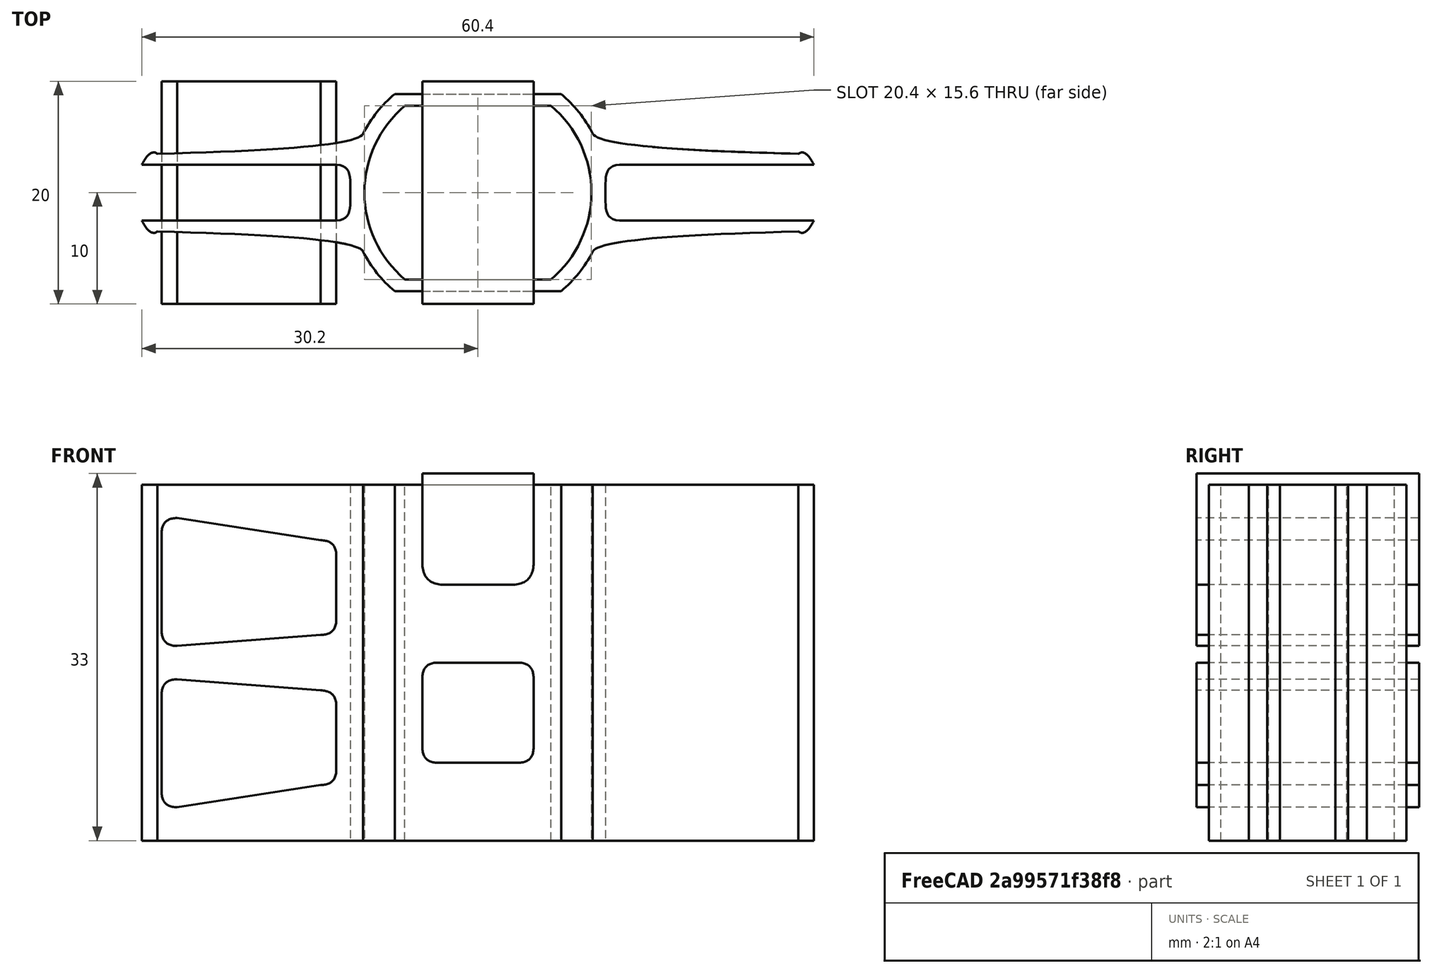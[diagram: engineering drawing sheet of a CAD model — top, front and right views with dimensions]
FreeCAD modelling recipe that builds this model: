
FCSTD DOCUMENT  (FreeCAD 0.19R0.19.2)
Label: 026
License: All rights reserved
LicenseURL: http://en.wikipedia.org/wiki/All_rights_reserved
objects: Sketcher::SketchObject×3, Part::Extrusion×3
note: 6 computed .brp shape members not serialized (recipe doc carries the construction recipe); baked Part::Feature solids carry a one-line shape summary decoded from their .brp

FEATURE [Sketcher::SketchObject] Sketch  label="main001"
  FullyConstrained = true
  sketch-geometry (80):
    g0: ArcOfCircle CenterX=-3.45031e-07 CenterY=0 CenterZ=0 NormalX=0 NormalY=0 NormalZ=1 AngleXU=0 Radius=10.2 StartAngle=5.4126 EndAngle=7.15377
    g1: ArcOfCircle CenterX=-3.45031e-07 CenterY=0 CenterZ=0 NormalX=0 NormalY=0 NormalZ=1 AngleXU=0 Radius=10.2 StartAngle=2.27101 EndAngle=4.01218
    g2: LineSegment StartX=-6.57267 StartY=7.8 StartZ=0 EndX=6.57267 EndY=7.8 EndZ=0
    g3: LineSegment StartX=-6.57267 StartY=-7.8 StartZ=0 EndX=6.57267 EndY=-7.8 EndZ=0
    g4: ArcOfCircle CenterX=-3.45031e-07 CenterY=0 CenterZ=0 NormalX=0 NormalY=0 NormalZ=1 AngleXU=0 Radius=11.6 StartAngle=2.27101 EndAngle=2.66709
    g5: ArcOfCircle CenterX=-3.45031e-07 CenterY=0 CenterZ=0 NormalX=0 NormalY=0 NormalZ=1 AngleXU=0 Radius=11.6 StartAngle=5.4126 EndAngle=5.80868
    g6: LineSegment StartX=-7.4748 StartY=8.87059 StartZ=0 EndX=7.4748 EndY=8.87059 EndZ=0
    g7: LineSegment StartX=-7.4748 StartY=-8.87059 StartZ=0 EndX=7.4748 EndY=-8.87059 EndZ=0
    g8: ArcOfCircle CenterX=-3.45031e-07 CenterY=0 CenterZ=0 NormalX=0 NormalY=0 NormalZ=1 AngleXU=0 Radius=11.6 StartAngle=3.6161 EndAngle=4.01218
    g9: ArcOfCircle CenterX=-3.45031e-07 CenterY=0 CenterZ=0 NormalX=0 NormalY=0 NormalZ=1 AngleXU=0 Radius=11.6 StartAngle=0.474503 EndAngle=0.870585
    g10: Circle CenterX=-28.8 CenterY=3.5 CenterZ=0 NormalX=0 NormalY=0 NormalZ=1 AngleXU=0 Radius=1
    g11: Circle CenterX=-10.9247 CenterY=3.9 CenterZ=0 NormalX=0 NormalY=0 NormalZ=1 AngleXU=0 Radius=1
    g12: Circle CenterX=-10.3184 CenterY=5.3 CenterZ=0 NormalX=0 NormalY=0 NormalZ=1 AngleXU=0 Radius=1
    g13: BSplineCurve PolesCount=3 KnotsCount=2 Degree=2 IsPeriodic=0
    g14: GeomPoint X=-28.8 Y=3.5 Z=0
    g15: GeomPoint X=-10.3184 Y=5.3 Z=0
    g16: Circle CenterX=28.8 CenterY=3.5 CenterZ=0 NormalX=0 NormalY=0 NormalZ=1 AngleXU=0 Radius=1
    g17: Circle CenterX=10.9247 CenterY=3.9 CenterZ=0 NormalX=0 NormalY=0 NormalZ=1 AngleXU=0 Radius=1
    g18: Circle CenterX=10.3184 CenterY=5.3 CenterZ=0 NormalX=0 NormalY=0 NormalZ=1 AngleXU=0 Radius=1
    g19: BSplineCurve PolesCount=3 KnotsCount=2 Degree=2 IsPeriodic=0
    g20: GeomPoint X=28.8 Y=3.5 Z=0
    g21: GeomPoint X=10.3184 Y=5.3 Z=0
    g22: Circle CenterX=-28.8 CenterY=-3.5 CenterZ=0 NormalX=0 NormalY=0 NormalZ=1 AngleXU=0 Radius=1
    g23: Circle CenterX=-10.9247 CenterY=-3.9 CenterZ=0 NormalX=0 NormalY=0 NormalZ=1 AngleXU=0 Radius=1
    g24: Circle CenterX=-10.3184 CenterY=-5.3 CenterZ=0 NormalX=0 NormalY=0 NormalZ=1 AngleXU=0 Radius=1
    g25: BSplineCurve PolesCount=3 KnotsCount=2 Degree=2 IsPeriodic=0
    g26: GeomPoint X=-28.8 Y=-3.5 Z=0
    g27: GeomPoint X=-10.3184 Y=-5.3 Z=0
    g28: Circle CenterX=28.8 CenterY=-3.5 CenterZ=0 NormalX=0 NormalY=0 NormalZ=1 AngleXU=0 Radius=1
    g29: Circle CenterX=10.9247 CenterY=-3.9 CenterZ=0 NormalX=0 NormalY=0 NormalZ=1 AngleXU=0 Radius=1
    g30: Circle CenterX=10.3184 CenterY=-5.3 CenterZ=0 NormalX=0 NormalY=0 NormalZ=1 AngleXU=0 Radius=1
    g31: BSplineCurve PolesCount=3 KnotsCount=2 Degree=2 IsPeriodic=0
    g32: GeomPoint X=28.8 Y=-3.5 Z=0
    g33: GeomPoint X=10.3184 Y=-5.3 Z=0
    g34-g38: Circle x5 (B-spline internal-alignment scaffolding for g39; pole/knot coordinates omitted)
    g39: BSplineCurve PolesCount=5 KnotsCount=3 Degree=3 IsPeriodic=0
    g40: GeomPoint X=12.7274 Y=2.5 Z=0
    g41: GeomPoint X=11.4637 Y=2.49999e-07 Z=0
    g42: GeomPoint X=12.7274 Y=-2.5 Z=0
    g43-g47: Circle x5 (B-spline internal-alignment scaffolding for g48; pole/knot coordinates omitted)
    g48: BSplineCurve PolesCount=5 KnotsCount=3 Degree=3 IsPeriodic=0
    g49: GeomPoint X=-12.7274 Y=2.5 Z=0
    g50: GeomPoint X=-11.4637 Y=2.50004e-07 Z=0
    g51: GeomPoint X=-12.7274 Y=-2.5 Z=0
    g52: LineSegment StartX=-30.2 StartY=-2.5 StartZ=0 EndX=-12.7274 EndY=-2.5 EndZ=0
    g53: LineSegment StartX=-30.2 StartY=2.5 StartZ=0 EndX=-12.7274 EndY=2.5 EndZ=0
    g54: LineSegment StartX=30.2 StartY=2.5 StartZ=0 EndX=12.7274 EndY=2.5 EndZ=0
    g55: LineSegment StartX=30.2 StartY=-2.5 StartZ=0 EndX=12.7274 EndY=-2.5 EndZ=0
    g56: Circle CenterX=-30.2 CenterY=2.5 CenterZ=0 NormalX=0 NormalY=0 NormalZ=1 AngleXU=0 Radius=1
    g57: Circle CenterX=-29.4304 CenterY=3.99253 CenterZ=0 NormalX=0 NormalY=0 NormalZ=1 AngleXU=0 Radius=1
    g58: Circle CenterX=-28.8 CenterY=3.5 CenterZ=0 NormalX=0 NormalY=0 NormalZ=1 AngleXU=0 Radius=1
    g59: BSplineCurve PolesCount=3 KnotsCount=2 Degree=2 IsPeriodic=0
    g60: GeomPoint X=-30.2 Y=2.5 Z=0
    g61: GeomPoint X=-28.8 Y=3.5 Z=0
    g62: Circle CenterX=30.2 CenterY=-2.5 CenterZ=0 NormalX=0 NormalY=0 NormalZ=1 AngleXU=0 Radius=1
    g63: Circle CenterX=29.4304 CenterY=-3.99253 CenterZ=0 NormalX=0 NormalY=0 NormalZ=1 AngleXU=0 Radius=1
    g64: Circle CenterX=28.8 CenterY=-3.5 CenterZ=0 NormalX=0 NormalY=0 NormalZ=1 AngleXU=0 Radius=1
    g65: BSplineCurve PolesCount=3 KnotsCount=2 Degree=2 IsPeriodic=0
    g66: GeomPoint X=30.2 Y=-2.5 Z=0
    g67: GeomPoint X=28.8 Y=-3.5 Z=0
    g68: Circle CenterX=30.2 CenterY=2.5 CenterZ=0 NormalX=0 NormalY=0 NormalZ=1 AngleXU=0 Radius=1
    g69: Circle CenterX=29.4304 CenterY=3.99253 CenterZ=0 NormalX=0 NormalY=0 NormalZ=1 AngleXU=0 Radius=1
    g70: Circle CenterX=28.8 CenterY=3.5 CenterZ=0 NormalX=0 NormalY=0 NormalZ=1 AngleXU=0 Radius=1
    g71: BSplineCurve PolesCount=3 KnotsCount=2 Degree=2 IsPeriodic=0
    g72: GeomPoint X=30.2 Y=2.5 Z=0
    g73: GeomPoint X=28.8 Y=3.5 Z=0
    g74: Circle CenterX=-30.2 CenterY=-2.5 CenterZ=0 NormalX=0 NormalY=0 NormalZ=1 AngleXU=0 Radius=1
    g75: Circle CenterX=-29.4304 CenterY=-3.99253 CenterZ=0 NormalX=0 NormalY=0 NormalZ=1 AngleXU=0 Radius=1
    g76: Circle CenterX=-28.8 CenterY=-3.5 CenterZ=0 NormalX=0 NormalY=0 NormalZ=1 AngleXU=0 Radius=1
    g77: BSplineCurve PolesCount=3 KnotsCount=2 Degree=2 IsPeriodic=0
    g78: GeomPoint X=-30.2 Y=-2.5 Z=0
    g79: GeomPoint X=-28.8 Y=-3.5 Z=0
  constraints (131):
    c: Block(g0)
    c: Equal(g0,g1)
    c: Coincident(g0,g1)
    c: Coincident(g2,g1)
    c: Coincident(g2,g0)
    c: Horizontal(g2)
    c: Coincident(g3,g1)
    c: Coincident(g3,g0)
    c: Horizontal(g3)
    c: Block(g2)
    c: Block(g3)
    c: Coincident(g4,g0)
    c: Coincident(g5,g0)
    c: Block(g5)
    c: Block(g4)
    c: Coincident(g6,g4)
    c: Coincident(g6,g9)
    c: Horizontal(g6)
    c: Coincident(g7,g8)
    c: Coincident(g7,g5)
    c: Horizontal(g7)
    c: Equal(g4,g8)
    c: Coincident(g4,g8)
    c: Equal(g5,g9)
    c: Coincident(g5,g9)
    c: Block(g8)
    c: Block(g9)
    c: Weight(g10) = 1
    c: Equal(g10,g11)
    c: Equal(g10,g12)
    c: Coincident(g13,g4)
    c: InternalAlignment(g10,g13)
    c: InternalAlignment(g11,g13)
    c: InternalAlignment(g12,g13)
    c: InternalAlignment(g14,g13)
    c: InternalAlignment(g15,g13)
    c: Weight(g16) = 1
    c: Equal(g16,g17)
    c: Equal(g16,g18)
    c: Coincident(g19,g9)
    c: InternalAlignment(g16,g19)
    c: InternalAlignment(g17,g19)
    c: InternalAlignment(g18,g19)
    c: InternalAlignment(g20,g19)
    c: InternalAlignment(g21,g19)
    c: Weight(g22) = 1
    c: Equal(g22,g23)
    c: Equal(g22,g24)
    c: Coincident(g25,g8)
    c: InternalAlignment(g22,g25)
    c: InternalAlignment(g23,g25)
    c: InternalAlignment(g24,g25)
    c: InternalAlignment(g26,g25)
    c: InternalAlignment(g27,g25)
    c: Weight(g28) = 1
    c: Equal(g28,g29)
    c: Equal(g28,g30)
    c: Coincident(g31,g5)
    c: InternalAlignment(g28,g31)
    c: InternalAlignment(g29,g31)
    c: InternalAlignment(g30,g31)
    c: InternalAlignment(g32,g31)
    c: InternalAlignment(g33,g31)
    c: Block(g19)
    c: Block(g13)
    c: Block(g31)
    c: Block(g25)
    c: Weight(g34) = 1
    c: Equal(g34, g35-g38) x4
    c: InternalAlignment(g34-g38 -> g39) x5
    c: InternalAlignment(g40,g39)
    c: InternalAlignment(g41,g39)
    c: InternalAlignment(g42,g39)
    c: Weight(g43) = 1
    c: Equal(g43,g44)
    c: Equal(g43,g45)
    c: Equal(g43,g46)
    c: InternalAlignment(g43-g47 -> g48) x5
    c: InternalAlignment(g49,g48)
    c: InternalAlignment(g50,g48)
    c: InternalAlignment(g51,g48)
    c: Block(g48)
    c: Block(g39)
    c: Coincident(g52,g48)
    c: Tangent(g52,g22)
    c: Coincident(g53,g48)
    c: Tangent(g53,g10)
    c: Coincident(g54,g39)
    c: Tangent(g54,g16)
    c: Coincident(g55,g39)
    c: Tangent(g55,g28)
    c: Weight(g56) = 1
    c: Equal(g56,g57)
    c: Equal(g56,g58)
    c: InternalAlignment(g56,g59)
    c: InternalAlignment(g57,g59)
    c: InternalAlignment(g58,g59)
    c: InternalAlignment(g60,g59)
    c: InternalAlignment(g61,g59)
    c: Weight(g62) = 1
    c: Equal(g62,g63)
    c: Equal(g62,g64)
    c: InternalAlignment(g62,g65)
    c: InternalAlignment(g63,g65)
    c: InternalAlignment(g64,g65)
    c: InternalAlignment(g66,g65)
    c: InternalAlignment(g67,g65)
    c: Weight(g68) = 1
    c: Equal(g68,g69)
    c: Equal(g68,g70)
    c: InternalAlignment(g68,g71)
    c: InternalAlignment(g69,g71)
    c: InternalAlignment(g70,g71)
    c: InternalAlignment(g72,g71)
    c: InternalAlignment(g73,g71)
    c: Block(g71)
    c: Block(g54)
    c: Block(g65)
    c: Block(g55)
    c: Weight(g74) = 1
    c: Equal(g74,g75)
    c: Equal(g74,g76)
    c: InternalAlignment(g74,g77)
    c: InternalAlignment(g75,g77)
    c: InternalAlignment(g76,g77)
    c: InternalAlignment(g78,g77)
    c: InternalAlignment(g79,g77)
    c: Block(g77)
    c: Block(g52)
    c: Block(g59)
    c: Block(g53)
FEATURE [Part::Extrusion] Extrude  label="main"
  Base = -> Sketch
  Dir = (0,0,1)
  DirMode = 2
  FaceMakerClass = Part::FaceMakerBullseye
  LengthFwd = 32
  LengthRev = 0
  Solid = true
  Symmetric = false
FEATURE [Sketcher::SketchObject] Sketch001  label="mainCollingAndStructuralHoles"
  FullyConstrained = true
  Placement = pos=(0,0,0) rot=(-1,0,0;4.71239rad)
  sketch-geometry (44):
    g0: Circle CenterX=-5 CenterY=2 CenterZ=0 NormalX=0 NormalY=0 NormalZ=1 AngleXU=0 Radius=1
    g1: Circle CenterX=-5 CenterY=0 CenterZ=0 NormalX=0 NormalY=0 NormalZ=1 AngleXU=0 Radius=1
    g2: Circle CenterX=-3 CenterY=4.6505e-12 CenterZ=0 NormalX=0 NormalY=0 NormalZ=1 AngleXU=0 Radius=1
    g3: BSplineCurve PolesCount=3 KnotsCount=2 Degree=2 IsPeriodic=0
    g4: GeomPoint X=-5 Y=2 Z=0
    g5: GeomPoint X=-3 Y=4.6505e-12 Z=0
    g6: Circle CenterX=5 CenterY=2 CenterZ=0 NormalX=0 NormalY=0 NormalZ=1 AngleXU=0 Radius=1
    g7: Circle CenterX=5 CenterY=4.6505e-12 CenterZ=0 NormalX=0 NormalY=0 NormalZ=1 AngleXU=0 Radius=1
    g8: Circle CenterX=3 CenterY=4.6505e-12 CenterZ=0 NormalX=0 NormalY=0 NormalZ=1 AngleXU=0 Radius=1
    g9: BSplineCurve PolesCount=3 KnotsCount=2 Degree=2 IsPeriodic=0
    g10: GeomPoint X=5 Y=2 Z=0
    g11: GeomPoint X=3 Y=4.6505e-12 Z=0
    g12: LineSegment StartX=5 StartY=2 StartZ=0 EndX=5 EndY=10 EndZ=0
    g13: LineSegment StartX=-5 StartY=2 StartZ=0 EndX=-5 EndY=10 EndZ=0
    g14: LineSegment StartX=-3 StartY=4.6505e-12 StartZ=0 EndX=3 EndY=4.6505e-12 EndZ=0
    g15: LineSegment StartX=-5 StartY=10 StartZ=0 EndX=5 EndY=10 EndZ=0
    g16: Circle CenterX=-3.6 CenterY=-7 CenterZ=0 NormalX=0 NormalY=0 NormalZ=1 AngleXU=0 Radius=1
    g17: Circle CenterX=-5 CenterY=-7 CenterZ=0 NormalX=0 NormalY=0 NormalZ=1 AngleXU=0 Radius=1
    g18: Circle CenterX=-5 CenterY=-8.4 CenterZ=0 NormalX=0 NormalY=0 NormalZ=1 AngleXU=0 Radius=1
    g19: BSplineCurve PolesCount=3 KnotsCount=2 Degree=2 IsPeriodic=0
    g20: GeomPoint X=-3.6 Y=-7 Z=0
    g21: GeomPoint X=-5 Y=-8.4 Z=0
    g22: Circle CenterX=5 CenterY=-8.4 CenterZ=0 NormalX=0 NormalY=0 NormalZ=1 AngleXU=0 Radius=1
    g23: Circle CenterX=5 CenterY=-7 CenterZ=0 NormalX=0 NormalY=0 NormalZ=1 AngleXU=0 Radius=1
    g24: Circle CenterX=3.6 CenterY=-7 CenterZ=0 NormalX=0 NormalY=0 NormalZ=1 AngleXU=0 Radius=1
    g25: BSplineCurve PolesCount=3 KnotsCount=2 Degree=2 IsPeriodic=0
    g26: GeomPoint X=5 Y=-8.4 Z=0
    g27: GeomPoint X=3.6 Y=-7 Z=0
    g28: Circle CenterX=-3.6 CenterY=-16 CenterZ=0 NormalX=0 NormalY=0 NormalZ=1 AngleXU=0 Radius=1
    g29: Circle CenterX=-5 CenterY=-16 CenterZ=0 NormalX=0 NormalY=0 NormalZ=1 AngleXU=0 Radius=1
    g30: Circle CenterX=-5 CenterY=-14.6 CenterZ=0 NormalX=0 NormalY=0 NormalZ=1 AngleXU=0 Radius=1
    g31: BSplineCurve PolesCount=3 KnotsCount=2 Degree=2 IsPeriodic=0
    g32: GeomPoint X=-3.6 Y=-16 Z=0
    g33: GeomPoint X=-5 Y=-14.6 Z=0
    g34: Circle CenterX=5 CenterY=-14.6 CenterZ=0 NormalX=0 NormalY=0 NormalZ=1 AngleXU=0 Radius=1
    g35: Circle CenterX=5 CenterY=-16 CenterZ=0 NormalX=0 NormalY=0 NormalZ=1 AngleXU=0 Radius=1
    g36: Circle CenterX=3.6 CenterY=-16 CenterZ=0 NormalX=0 NormalY=0 NormalZ=1 AngleXU=0 Radius=1
    g37: BSplineCurve PolesCount=3 KnotsCount=2 Degree=2 IsPeriodic=0
    g38: GeomPoint X=5 Y=-14.6 Z=0
    g39: GeomPoint X=3.6 Y=-16 Z=0
    g40: LineSegment StartX=-3.6 StartY=-7 StartZ=0 EndX=3.6 EndY=-7 EndZ=0
    g41: LineSegment StartX=-5 StartY=-8.4 StartZ=0 EndX=-5 EndY=-14.6 EndZ=0
    g42: LineSegment StartX=-3.6 StartY=-16 StartZ=0 EndX=3.6 EndY=-16 EndZ=0
    g43: LineSegment StartX=5 StartY=-14.6 StartZ=0 EndX=5 EndY=-8.4 EndZ=0
  constraints (79):
    c: Weight(g0) = 1
    c: Equal(g0,g1)
    c: Equal(g0,g2)
    c: InternalAlignment(g0,g3)
    c: InternalAlignment(g1,g3)
    c: InternalAlignment(g2,g3)
    c: InternalAlignment(g4,g3)
    c: InternalAlignment(g5,g3)
    c: Weight(g6) = 1
    c: Equal(g6,g7)
    c: Equal(g6,g8)
    c: InternalAlignment(g6,g9)
    c: InternalAlignment(g7,g9)
    c: InternalAlignment(g8,g9)
    c: InternalAlignment(g10,g9)
    c: InternalAlignment(g11,g9)
    c: Block(g3)
    c: Coincident(g13,g3)
    c: Block(g9)
    c: Coincident(g12,g9)
    c: Vertical(g12)
    c: Block(g12)
    c: Block(g13)
    c: Coincident(g14,g3)
    c: Coincident(g14,g9)
    c: Horizontal(g14)
    c: Coincident(g15,g13)
    c: Coincident(g15,g12)
    c: Horizontal(g15)
    c: Distance(g12) = 8
    c: Distance(g15) = 10
    c: Weight(g16) = 1
    c: Equal(g16,g17)
    c: Equal(g16,g18)
    c: InternalAlignment(g16,g19)
    c: InternalAlignment(g17,g19)
    c: InternalAlignment(g18,g19)
    c: InternalAlignment(g20,g19)
    c: InternalAlignment(g21,g19)
    c: Weight(g22) = 1
    c: Equal(g22,g23)
    c: Equal(g22,g24)
    c: InternalAlignment(g22,g25)
    c: InternalAlignment(g23,g25)
    c: InternalAlignment(g24,g25)
    c: InternalAlignment(g26,g25)
    c: InternalAlignment(g27,g25)
    c: Weight(g28) = 1
    c: Equal(g28,g29)
    c: Equal(g28,g30)
    c: InternalAlignment(g28,g31)
    c: InternalAlignment(g29,g31)
    c: InternalAlignment(g30,g31)
    c: InternalAlignment(g32,g31)
    c: InternalAlignment(g33,g31)
    c: Weight(g34) = 1
    c: Equal(g34,g35)
    c: Equal(g34,g36)
    c: InternalAlignment(g34,g37)
    c: InternalAlignment(g35,g37)
    c: InternalAlignment(g36,g37)
    c: InternalAlignment(g38,g37)
    c: InternalAlignment(g39,g37)
    c: Block(g25)
    c: Block(g37)
    c: Block(g31)
    c: Block(g19)
    c: Coincident(g40,g19)
    c: Coincident(g40,g25)
    c: Horizontal(g40)
    c: Coincident(g41,g19)
    c: Coincident(g41,g31)
    c: Vertical(g41)
    c: Coincident(g42,g31)
    c: Coincident(g42,g37)
    c: Horizontal(g42)
    c: Coincident(g43,g37)
    c: Coincident(g43,g25)
    c: Vertical(g43)
FEATURE [Part::Extrusion] Extrude001  label="mainCollingAndStructuralHoles001"
  Base = -> Sketch001
  Dir = (0,-1,3e-16)
  DirMode = 2
  FaceMakerClass = Part::FaceMakerBullseye
  LengthFwd = 20
  LengthRev = 0
  Placement = pos=(0,10,23) rot=(0,0,1;0rad)
  Solid = true
  Symmetric = false
FEATURE [Sketcher::SketchObject] Sketch002
  FullyConstrained = true
  Placement = pos=(0,0,0) rot=(-1,0,0;4.71239rad)
  sketch-geometry (55):
    g0: LineSegment StartX=-28.43 StartY=13.1 StartZ=0 EndX=-28.43 EndY=4.4 EndZ=0
    g1: LineSegment StartX=-28.43 StartY=27.6 StartZ=0 EndX=-28.43 EndY=18.9 EndZ=0
    g2: LineSegment StartX=-12.73 StartY=25.6 StartZ=0 EndX=-12.73 EndY=19.9 EndZ=0
    g3: LineSegment StartX=-12.73 StartY=12.1 StartZ=0 EndX=-12.73 EndY=6.4 EndZ=0
    g4: Circle CenterX=-28.43 CenterY=27.6 CenterZ=0 NormalX=0 NormalY=0 NormalZ=1 AngleXU=0 Radius=1
    g5: Circle CenterX=-28.43 CenterY=29 CenterZ=0 NormalX=0 NormalY=0 NormalZ=1 AngleXU=0 Radius=1
    g6: Circle CenterX=-27.03 CenterY=29 CenterZ=0 NormalX=0 NormalY=0 NormalZ=1 AngleXU=0 Radius=1
    g7: BSplineCurve PolesCount=3 KnotsCount=2 Degree=2 IsPeriodic=0
    g8: GeomPoint X=-28.43 Y=27.6 Z=0
    g9: GeomPoint X=-27.03 Y=29 Z=0
    g10: Circle CenterX=-14.13 CenterY=27 CenterZ=0 NormalX=0 NormalY=0 NormalZ=1 AngleXU=0 Radius=1
    g11: Circle CenterX=-12.73 CenterY=27 CenterZ=0 NormalX=0 NormalY=0 NormalZ=1 AngleXU=0 Radius=1
    g12: Circle CenterX=-12.73 CenterY=25.6 CenterZ=0 NormalX=0 NormalY=0 NormalZ=1 AngleXU=0 Radius=1
    g13: BSplineCurve PolesCount=3 KnotsCount=2 Degree=2 IsPeriodic=0
    g14: GeomPoint X=-14.13 Y=27 Z=0
    g15: GeomPoint X=-12.73 Y=25.6 Z=0
    g16: Circle CenterX=-14.13 CenterY=18.5 CenterZ=0 NormalX=0 NormalY=0 NormalZ=1 AngleXU=0 Radius=1
    g17: Circle CenterX=-12.73 CenterY=18.5 CenterZ=0 NormalX=0 NormalY=0 NormalZ=1 AngleXU=0 Radius=1
    g18: Circle CenterX=-12.73 CenterY=19.9 CenterZ=0 NormalX=0 NormalY=0 NormalZ=1 AngleXU=0 Radius=1
    g19: BSplineCurve PolesCount=3 KnotsCount=2 Degree=2 IsPeriodic=0
    g20: GeomPoint X=-14.13 Y=18.5 Z=0
    g21: GeomPoint X=-12.73 Y=19.9 Z=0
    g22: Circle CenterX=-27.03 CenterY=17.5 CenterZ=0 NormalX=0 NormalY=0 NormalZ=1 AngleXU=0 Radius=1
    g23: Circle CenterX=-28.43 CenterY=17.5 CenterZ=0 NormalX=0 NormalY=0 NormalZ=1 AngleXU=0 Radius=1
    g24: Circle CenterX=-28.43 CenterY=18.9 CenterZ=0 NormalX=0 NormalY=0 NormalZ=1 AngleXU=0 Radius=1
    g25: BSplineCurve PolesCount=3 KnotsCount=2 Degree=2 IsPeriodic=0
    g26: GeomPoint X=-27.03 Y=17.5 Z=0
    g27: GeomPoint X=-28.43 Y=18.9 Z=0
    g28: Circle CenterX=-27.03 CenterY=14.5 CenterZ=0 NormalX=0 NormalY=0 NormalZ=1 AngleXU=0 Radius=1
    g29: Circle CenterX=-28.43 CenterY=14.5 CenterZ=0 NormalX=0 NormalY=0 NormalZ=1 AngleXU=0 Radius=1
    g30: Circle CenterX=-28.43 CenterY=13.1 CenterZ=0 NormalX=0 NormalY=0 NormalZ=1 AngleXU=0 Radius=1
    g31: BSplineCurve PolesCount=3 KnotsCount=2 Degree=2 IsPeriodic=0
    g32: GeomPoint X=-27.03 Y=14.5 Z=0
    g33: GeomPoint X=-28.43 Y=13.1 Z=0
    g34: Circle CenterX=-14.13 CenterY=13.5 CenterZ=0 NormalX=0 NormalY=0 NormalZ=1 AngleXU=0 Radius=1
    g35: Circle CenterX=-12.73 CenterY=13.5 CenterZ=0 NormalX=0 NormalY=0 NormalZ=1 AngleXU=0 Radius=1
    g36: Circle CenterX=-12.73 CenterY=12.1 CenterZ=0 NormalX=0 NormalY=0 NormalZ=1 AngleXU=0 Radius=1
    g37: BSplineCurve PolesCount=3 KnotsCount=2 Degree=2 IsPeriodic=0
    g38: GeomPoint X=-14.13 Y=13.5 Z=0
    g39: GeomPoint X=-12.73 Y=12.1 Z=0
    g40: Circle CenterX=-27.03 CenterY=3 CenterZ=0 NormalX=0 NormalY=0 NormalZ=1 AngleXU=0 Radius=1
    g41: Circle CenterX=-28.43 CenterY=3 CenterZ=0 NormalX=0 NormalY=0 NormalZ=1 AngleXU=0 Radius=1
    g42: Circle CenterX=-28.43 CenterY=4.4 CenterZ=0 NormalX=0 NormalY=0 NormalZ=1 AngleXU=0 Radius=1
    g43: BSplineCurve PolesCount=3 KnotsCount=2 Degree=2 IsPeriodic=0
    g44: GeomPoint X=-28.43 Y=4.4 Z=0
    g45: Circle CenterX=-14.13 CenterY=5 CenterZ=0 NormalX=0 NormalY=0 NormalZ=1 AngleXU=0 Radius=1
    g46: Circle CenterX=-12.73 CenterY=5 CenterZ=0 NormalX=0 NormalY=0 NormalZ=1 AngleXU=0 Radius=1
    g47: Circle CenterX=-12.73 CenterY=6.4 CenterZ=0 NormalX=0 NormalY=0 NormalZ=1 AngleXU=0 Radius=1
    g48: BSplineCurve PolesCount=3 KnotsCount=2 Degree=2 IsPeriodic=0
    g49: GeomPoint X=-14.13 Y=5 Z=0
    g50: GeomPoint X=-12.73 Y=6.4 Z=0
    g51: LineSegment StartX=-27.03 StartY=3 StartZ=0 EndX=-14.13 EndY=5 EndZ=0
    g52: LineSegment StartX=-27.03 StartY=14.5 StartZ=0 EndX=-14.13 EndY=13.5 EndZ=0
    g53: LineSegment StartX=-27.03 StartY=17.5 StartZ=0 EndX=-14.13 EndY=18.5 EndZ=0
    g54: LineSegment StartX=-27.03 StartY=29 StartZ=0 EndX=-14.13 EndY=27 EndZ=0
  constraints (91):
    c: Distance(g0) = 8.7
    c: Vertical(g0)
    c: Equal(g0,g1) = 8.7
    c: Vertical(g1)
    c: Vertical(g2)
    c: Distance(g2) = 5.7
    c: Vertical(g3)
    c: Equal(g2,g3) = 7.1
    c: Weight(g4) = 1
    c: Equal(g4,g5)
    c: Equal(g4,g6)
    c: InternalAlignment(g4,g7)
    c: InternalAlignment(g5,g7)
    c: InternalAlignment(g6,g7)
    c: InternalAlignment(g8,g7)
    c: InternalAlignment(g9,g7)
    c: Weight(g10) = 1
    c: Equal(g10,g11)
    c: Equal(g10,g12)
    c: InternalAlignment(g10,g13)
    c: InternalAlignment(g11,g13)
    c: InternalAlignment(g12,g13)
    c: InternalAlignment(g14,g13)
    c: InternalAlignment(g15,g13)
    c: Weight(g16) = 1
    c: Equal(g16,g17)
    c: Equal(g16,g18)
    c: Coincident(g19,g2)
    c: InternalAlignment(g16,g19)
    c: InternalAlignment(g17,g19)
    c: InternalAlignment(g18,g19)
    c: InternalAlignment(g20,g19)
    c: InternalAlignment(g21,g19)
    c: Weight(g22) = 1
    c: Equal(g22,g23)
    c: Equal(g22,g24)
    c: Coincident(g25,g1)
    c: InternalAlignment(g22,g25)
    c: InternalAlignment(g23,g25)
    c: InternalAlignment(g24,g25)
    c: InternalAlignment(g26,g25)
    c: InternalAlignment(g27,g25)
    c: Weight(g28) = 1
    c: Equal(g28,g29)
    c: Equal(g28,g30)
    c: Coincident(g31,g0)
    c: InternalAlignment(g28,g31)
    c: InternalAlignment(g29,g31)
    c: InternalAlignment(g30,g31)
    c: InternalAlignment(g32,g31)
    c: InternalAlignment(g33,g31)
    c: Weight(g34) = 1
    c: Equal(g34,g35)
    c: Equal(g34,g36)
    c: Coincident(g37,g3)
    c: InternalAlignment(g34,g37)
    c: InternalAlignment(g35,g37)
    c: InternalAlignment(g36,g37)
    c: InternalAlignment(g38,g37)
    c: InternalAlignment(g39,g37)
    c: Weight(g40) = 1
    c: Equal(g40,g41)
    c: Equal(g40,g42)
    c: InternalAlignment(g40,g43)
    c: InternalAlignment(g41,g43)
    c: InternalAlignment(g42,g43)
    c: InternalAlignment(g44,g43)
    c: Weight(g45) = 1
    c: Equal(g45,g46)
    c: Equal(g45,g47)
    c: InternalAlignment(g45,g48)
    c: InternalAlignment(g46,g48)
    c: InternalAlignment(g47,g48)
    c: InternalAlignment(g49,g48)
    c: InternalAlignment(g50,g48)
    c: Block(g54)
    c: Block(g53)
    c: Block(g52)
    c: Block(g51)
    c: Block(g43)
    c: Block(g2)
    c: Block(g19)
    c: Block(g13)
    c: Block(g7)
    c: Block(g1)
    c: Block(g25)
    c: Block(g3)
    c: Block(g37)
    c: Block(g48)
    c: Block(g0)
    c: Block(g31)
FEATURE [Part::Extrusion] Extrude002
  Base = -> Sketch002
  Dir = (0,-1,3e-16)
  DirMode = 2
  FaceMakerClass = Part::FaceMakerBullseye
  LengthFwd = 20
  LengthRev = 0
  Placement = pos=(0,10,0) rot=(0,0,1;0rad)
  Solid = true
  Symmetric = false
